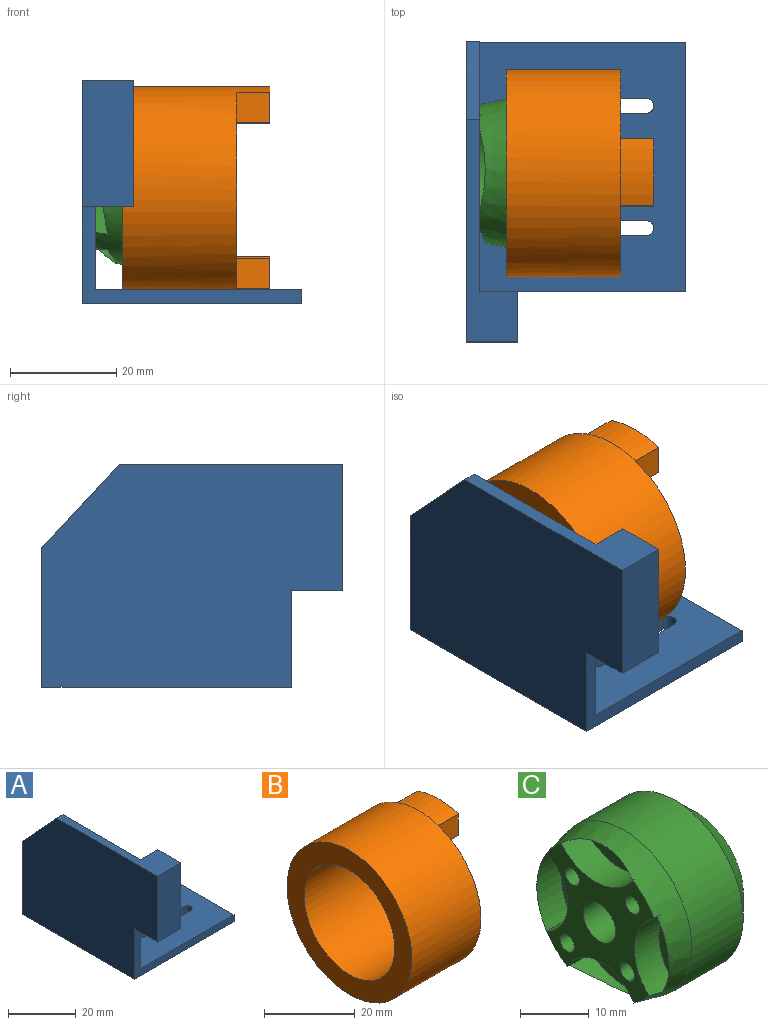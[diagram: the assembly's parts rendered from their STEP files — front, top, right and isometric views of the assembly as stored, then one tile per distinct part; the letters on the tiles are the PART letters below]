
ASSEMBLY  parts=3 mates=2
PART A: 21 faces, bbox 41.4x56.5x41.9 mm
  f0: plane 41.94x9.69mm, normal (0,0,1), area 174.6mm2, adj f2,f7,f16,f17,f19,f20
  f1: plane 41.43x26.24mm, normal (0,1,0), area 165.4mm2, adj f2,f3,f4,f6,f7,f16
  f2: plane 46.99x39.37mm, normal (1,0,0), area 1735.8mm2, adj f0,f1,f4,f5,f16,f17
  f3: plane 46.99x41.43mm, normal (0,0,-1), area 1826.1mm2, adj f1,f5,f6,f7,f8,f9,f10,f11
  f4: plane 46.99x38.89mm, normal (0,0,1), area 1706.7mm2, adj f1,f2,f5,f6,f8,f9,f10,f11
  f5: plane 41.43x18.15mm, normal (0,-1,0), area 144.9mm2, adj f2,f3,f4,f6,f7,f18
  f6: plane 46.99x2.54mm, normal (1,0,0), area 119.4mm2, adj f1,f3,f4,f5
  f7: plane 56.51x41.91mm, normal (-1,0,0), area 2081.4mm2, adj f0,f1,f3,f5,f16,f18,f20
  f8: cylinder r=1.42mm len=2.83mm, axis (0,0,-1), area 11.3mm2, adj f3,f4,f9,f11
  f9: plane 19.05x2.54mm, normal (0,-1,0), area 48.4mm2, adj f3,f4,f8,f10
  f10: cylinder r=1.42mm len=2.83mm, axis (0,0,-1), area 11.3mm2, adj f3,f4,f9,f11
  f11: plane 19.05x2.54mm, normal (0,1,0), area 48.4mm2, adj f3,f4,f8,f10
  f12: plane 19.05x2.54mm, normal (0,-1,0), area 48.4mm2, adj f3,f4,f13,f15
  f13: cylinder r=1.42mm len=2.83mm, axis (0,0,-1), area 11.3mm2, adj f3,f4,f12,f14
  f14: plane 19.05x2.54mm, normal (0,1,0), area 48.4mm2, adj f3,f4,f13,f15
  f15: cylinder r=1.42mm len=2.83mm, axis (0,0,-1), area 11.3mm2, adj f3,f4,f12,f14
  f16: plane 15.67x14.57mm, normal (0,0.73,0.68), area 54.3mm2, adj f0,f1,f2,f7
  f17: plane 23.76x7.15mm, normal (0,1,0), area 170mm2, adj f0,f2,f18,f19
  f18: plane 9.69x9.52mm, normal (0,0,-1), area 92.3mm2, adj f5,f7,f17,f19,f20
  f19: plane 23.76x9.52mm, normal (1,0,0), area 226.2mm2, adj f0,f17,f18,f20
  f20: plane 23.76x9.69mm, normal (0,-1,0), area 230.4mm2, adj f0,f7,f18,f19
PART B: 17 faces, bbox 27.9x39x39 mm
  f0: plane 37.04x13.11mm, normal (1,0,0), area 210.7mm2, adj f2,f4,f8,f12
  f1: plane 37.34x13.54mm, normal (1,0,0), area 215.6mm2, adj f2,f4,f6,f14
  f2: cylinder r=19.5mm len=39mm, axis (-1,0,0), area 2645.3mm2, adj f0,f1,f3,f9,f11
  f3: plane 39x39mm, normal (-1,0,0), area 565.6mm2, adj f2,f4
  f4: cylinder r=14.15mm len=28.3mm, axis (-1,0,0), area 1919.5mm2, adj f0,f1,f3,f5,f16
  f5: plane 12.7x1.61mm, normal (-1,0,0), area 0.4mm2, adj f4,f7
  f6: plane 6.26x5.76mm, normal (0,-1,0), area 36.1mm2, adj f1,f7,f9,f10
  f7: cylinder r=14.5mm len=12.7mm, axis (-1,0,0), area 82.3mm2, adj f5,f6,f8,f10
  f8: plane 6.26x5.83mm, normal (0,1,0), area 36.5mm2, adj f0,f7,f9,f10
  f9: cylinder r=19.45mm len=12.7mm, axis (-1,0,0), area 81mm2, adj f2,f6,f8,f10
  f10: plane 12.7x6.97mm, normal (1,0,0), area 70.1mm2, adj f6,f7,f8,f9
  f11: cylinder r=19.39mm len=12.7mm, axis (-1,0,0), area 81mm2, adj f2,f12,f14,f15
  f12: plane 6.26x5.83mm, normal (0,1,0), area 36.5mm2, adj f0,f11,f13,f15
  f13: cylinder r=14.35mm len=12.7mm, axis (-1,0,0), area 82.4mm2, adj f12,f14,f15,f16
  f14: plane 6.26x5.76mm, normal (0,-1,0), area 36.1mm2, adj f1,f11,f13,f15
  f15: plane 12.7x6.97mm, normal (1,0,0), area 70mm2, adj f11,f12,f13,f14
  f16: plane 12.7x1.61mm, normal (-1,0,0), area 0.2mm2, adj f4,f13
PART C: 28 faces, bbox 22x28x28 mm
  f0: cylinder r=14mm len=28mm, axis (-1,0,0), area 928.5mm2, adj f2,f6
  f1: plane 19.11x19.11mm, normal (1,0,0), area 217.5mm2, adj f2,f3
  f2: cone r=9.55mm half-angle=45deg, axis (-1,0,0), area 465.2mm2, adj f0,f1
  f3: cylinder r=4.7mm len=9.4mm, axis (-1,0,0), area 59mm2, adj f1,f4
  f4: plane 9.4x9.4mm, normal (1,0,0), area 35.1mm2, adj f3,f27
  f5: plane 22.07x22.03mm, normal (-1,0,0), area 224.5mm2, adj f6,f8,f10,f12,f14,f16,f19,f22
  f6: cone r=12.89mm half-angle=12.5deg, axis (1,0,0), area 356.2mm2, adj f0,f5,f15,f18,f21,f22,f24,f25
  f7: cone r=1.45mm half-angle=59deg, axis (-1,0,0), area 7.7mm2, adj f8
  f8: cylinder r=1.45mm len=2.9mm, axis (-1,0,0), area 23.1mm2, adj f5,f7
  f9: cone r=1.45mm half-angle=59deg, axis (-1,0,0), area 7.7mm2, adj f10
  f10: cylinder r=1.45mm len=2.9mm, axis (-1,0,0), area 23.1mm2, adj f5,f9
  f11: cone r=1.45mm half-angle=59deg, axis (-1,0,0), area 7.7mm2, adj f12
  f12: cylinder r=1.45mm len=2.9mm, axis (-1,0,0), area 23.1mm2, adj f5,f11
  f13: cone r=1.45mm half-angle=59deg, axis (-1,0,0), area 7.7mm2, adj f14
  f14: cylinder r=1.45mm len=2.9mm, axis (-1,0,0), area 23.1mm2, adj f5,f13
  f15: cylinder r=11.93mm len=14.73mm, axis (-1,0,0), area 68.3mm2, adj f6,f16,f17
  f16: cylinder r=9.19mm len=14.73mm, axis (-1,0,0), area 85.6mm2, adj f5,f15,f17
  f17: plane 14.73x6.28mm, normal (-1,0,0), area 64mm2, adj f15,f16
  f18: cylinder r=12.89mm len=13.89mm, axis (-1,0,0), area 73.3mm2, adj f6,f19,f20
  f19: cylinder r=7.73mm len=13.89mm, axis (-1,0,0), area 86.3mm2, adj f5,f18,f20
  f20: plane 13.89x6.36mm, normal (-1,0,0), area 62.2mm2, adj f18,f19
  f21: cylinder r=13.47mm len=14.73mm, axis (-1,0,0), area 58.5mm2, adj f6,f22,f23
  f22: cylinder r=9.19mm len=14.73mm, axis (-1,0,0), area 85mm2, adj f5,f6,f21,f23
  f23: plane 14.73x5.93mm, normal (-1,0,0), area 60.3mm2, adj f21,f22
  f24: cylinder r=10.82mm len=13.89mm, axis (-1,0,0), area 29.8mm2, adj f6,f25,f26
  f25: cylinder r=7.73mm len=13.89mm, axis (-1,0,0), area 85.7mm2, adj f5,f6,f24,f26
  f26: plane 13.89x6.86mm, normal (-1,0,0), area 67.1mm2, adj f24,f25
  f27: cylinder r=3.3mm len=22mm, axis (-1,0,0), area 456.4mm2, adj f4,f5
PLACE A t=(-67.52,-43.96,19.37)mm
PLACE B t=(-59.98,-11.73,-32.54)mm
PLACE C t=(-59.98,-11.73,-14.63)mm
MATE fastened C.f0 <-> A.f2  axis (-1,0,0) through (-64.98,-11.73,-14.63)mm
MATE fastened B.f2 <-> C.f0  axis (-1,0,0) through (-59.98,-11.73,-14.63)mm
